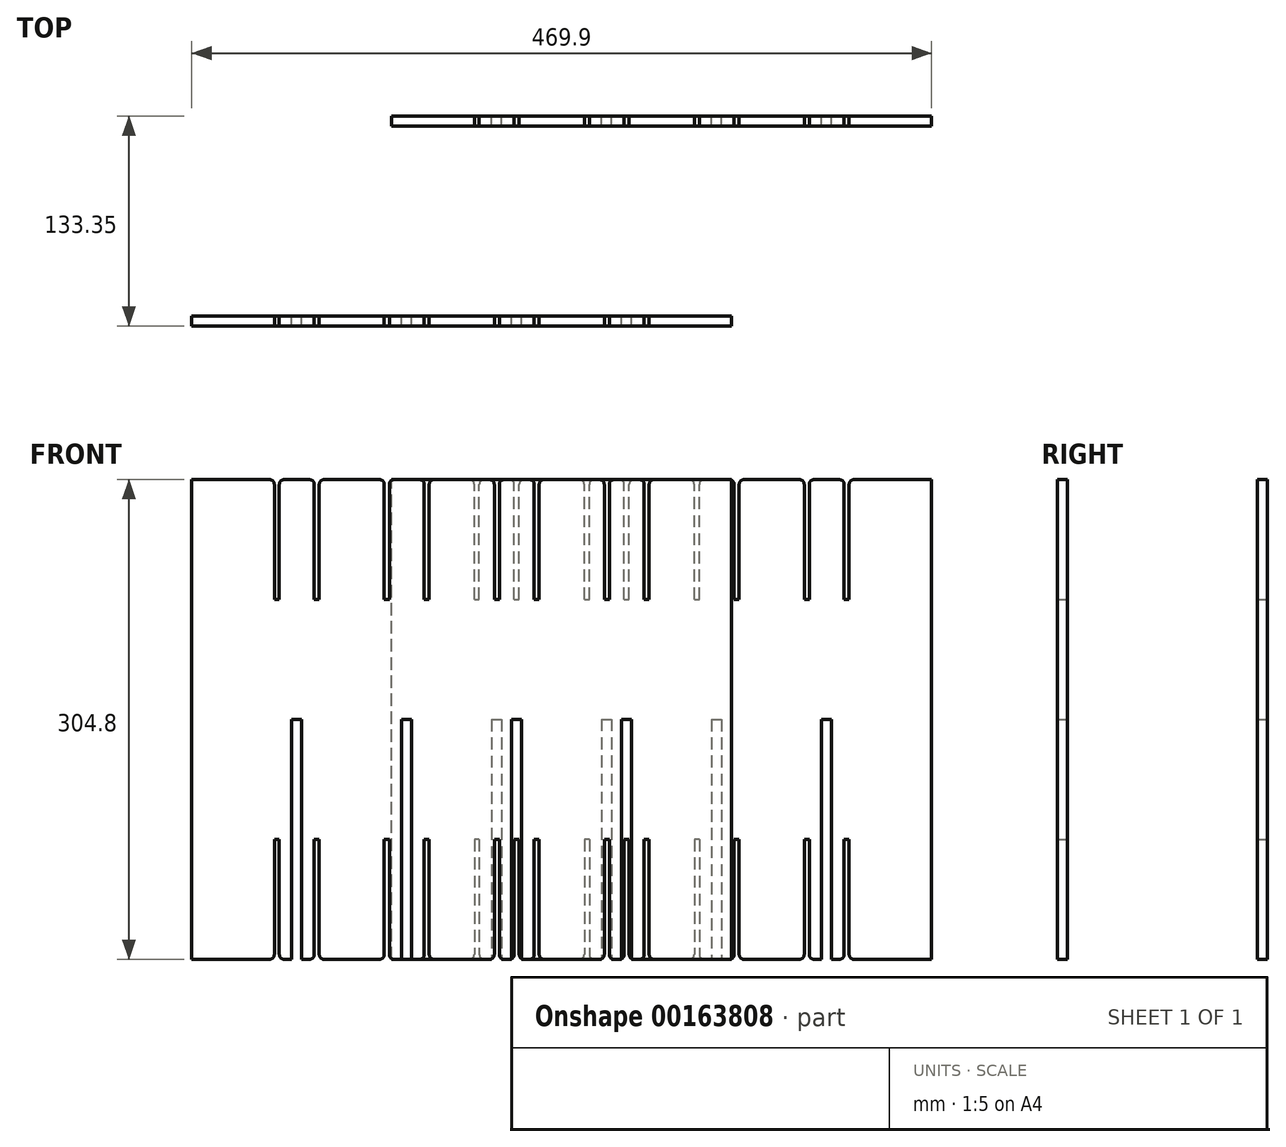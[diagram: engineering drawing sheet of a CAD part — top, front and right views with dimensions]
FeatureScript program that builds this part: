
annotation { "Feature Type Name" : "Feature", "Feature Type Description" : "" }
export const myFeature = defineFeature(function(context is Context, id is Id, definition is map)
    precondition{}
    {
        {
            var Q0;
            Q0=qCreatedBy(makeId("Front.planeOp"),FACE);
            var sketch = newSketch(context, id + "F0", { "sketchPlane" : qUnion([Q0])});
            skLineSegment(sketch, "E0.top", {"start": v(171.45, 164.84) * mm, "end": v(122.22, 164.84) * mm});
            skLineSegment(sketch, "E0.left", {"start": v(171.45, -139.96) * mm, "end": v(171.45, 164.84) * mm});
            skLineSegment(sketch, "E0.right", {"start": v(-171.45, -139.96) * mm, "end": v(-171.45, 164.84) * mm});
            skLineSegment(sketch, "E1", {"start": v(-171.45, -139.96) * mm, "end": v(-122.22, -139.96) * mm});
            skLineSegment(sketch, "E2", {"start": v(0, 0) * mm, "end": v(0, -139.96) * mm, "construction": true});
            skLineSegment(sketch, "E3.0", {"start": v(-31.75, 12.5) * mm, "end": v(-31.75, -139.96) * mm});
            skLineSegment(sketch, "E4.0", {"start": v(31.75, 12.46) * mm, "end": v(31.75, -139.96) * mm});
            skLineSegment(sketch, "E5.0", {"start": v(-38.1, 12.5) * mm, "end": v(-38.1, -139.96) * mm});
            skLineSegment(sketch, "E6.0", {"start": v(38.1, 12.46) * mm, "end": v(38.1, -139.96) * mm});
            skLineSegment(sketch, "E7.0", {"start": v(-101.6, 12.44) * mm, "end": v(-101.6, -139.96) * mm});
            skLineSegment(sketch, "E8.0", {"start": v(101.6, 12.32) * mm, "end": v(101.6, -139.96) * mm});
            skLineSegment(sketch, "E9.0", {"start": v(107.95, 12.32) * mm, "end": v(107.95, -139.96) * mm});
            skLineSegment(sketch, "E10.0", {"start": v(-107.95, 12.44) * mm, "end": v(-107.95, -139.96) * mm});
            skLineSegment(sketch, "E11", {"start": v(-107.95, 12.44) * mm, "end": v(-101.6, 12.44) * mm});
            skLineSegment(sketch, "E12", {"start": v(-38.1, 12.5) * mm, "end": v(-31.75, 12.5) * mm});
            skLineSegment(sketch, "E13", {"start": v(31.75, 12.46) * mm, "end": v(38.1, 12.46) * mm});
            skLineSegment(sketch, "E14", {"start": v(101.6, 12.32) * mm, "end": v(107.95, 12.32) * mm});
            skLineSegment(sketch, "E15.trimOffspring", {"start": v(-101.6, -139.96) * mm, "end": v(-96.85, -139.96) * mm});
            skLineSegment(sketch, "E16.trimOffspring", {"start": v(-31.75, -139.96) * mm, "end": v(-27, -139.96) * mm});
            skLineSegment(sketch, "E17.trimOffspring", {"start": v(38.1, -139.96) * mm, "end": v(42.85, -139.96) * mm});
            skLineSegment(sketch, "E18.trimOffspring", {"start": v(107.95, -139.96) * mm, "end": v(112.7, -139.96) * mm});
            skLineSegment(sketch, "E19", {"start": v(-104.77, 12.44) * mm, "end": v(-104.78, 164.84) * mm, "construction": true});
            skLineSegment(sketch, "E20", {"start": v(-34.93, 12.5) * mm, "end": v(-34.93, 164.84) * mm, "construction": true});
            skLineSegment(sketch, "E21", {"start": v(34.92, 12.46) * mm, "end": v(34.92, 164.84) * mm, "construction": true});
            skLineSegment(sketch, "E22", {"start": v(104.77, 12.32) * mm, "end": v(104.77, 164.84) * mm, "construction": true});
            skLineSegment(sketch, "E23.0", {"start": v(-93.68, 88.64) * mm, "end": v(-93.68, 161.67) * mm});
            skLineSegment(sketch, "E24.0", {"start": v(-115.87, 88.64) * mm, "end": v(-115.87, 161.67) * mm});
            skLineSegment(sketch, "E25.0", {"start": v(-119.05, 88.64) * mm, "end": v(-119.05, 161.67) * mm});
            skLineSegment(sketch, "E26.0", {"start": v(-90.5, 88.64) * mm, "end": v(-90.5, 161.67) * mm});
            skLineSegment(sketch, "E27.top", {"start": v(-119.05, 88.64) * mm, "end": v(-115.87, 88.64) * mm});
            skLineSegment(sketch, "E28.trimOffspring", {"start": v(-93.68, 88.64) * mm, "end": v(-90.5, 88.64) * mm});
            skLineSegment(sketch, "E29.trimOffspring", {"start": v(-96.85, 164.84) * mm, "end": v(-112.7, 164.84) * mm});
            skLineSegment(sketch, "E30.trimOffspring", {"start": v(-122.22, 164.84) * mm, "end": v(-171.45, 164.84) * mm});
            skPoint(sketch, "E31.visualSharp", {"position": v(-119.05, 164.84) * mm});
            skArc(sketch, "E31.filletArc", {"start": v(-119.05, 161.67) * mm, "mid": v(-119.98, 163.91) * mm, "end": v(-122.22, 164.84) * mm});
            skPoint(sketch, "E32.visualSharp", {"position": v(-115.87, 164.84) * mm});
            skArc(sketch, "E32.filletArc", {"start": v(-112.7, 164.84) * mm, "mid": v(-114.94, 163.91) * mm, "end": v(-115.87, 161.67) * mm});
            skPoint(sketch, "E33.visualSharp", {"position": v(-93.68, 164.84) * mm});
            skArc(sketch, "E33.filletArc", {"start": v(-93.68, 161.67) * mm, "mid": v(-94.6, 163.91) * mm, "end": v(-96.85, 164.84) * mm});
            skPoint(sketch, "E34.visualSharp", {"position": v(-90.5, 164.84) * mm});
            skArc(sketch, "E34.filletArc", {"start": v(-87.33, 164.84) * mm, "mid": v(-89.57, 163.91) * mm, "end": v(-90.5, 161.67) * mm});
            skLineSegment(sketch, "E35", {"start": v(-90.5, 88.64) * mm, "end": v(171.45, 88.64) * mm});
            skLineSegment(sketch, "E36.1.0.0", {"start": v(-49.2, 88.64) * mm, "end": v(-49.2, 161.67) * mm});
            skLineSegment(sketch, "E36.1.0.1", {"start": v(-46.02, 88.64) * mm, "end": v(-46.02, 161.67) * mm});
            skLineSegment(sketch, "E36.1.0.2", {"start": v(-23.83, 88.64) * mm, "end": v(-23.83, 161.67) * mm});
            skLineSegment(sketch, "E36.1.0.3", {"start": v(-20.65, 88.64) * mm, "end": v(-20.65, 161.67) * mm});
            skLineSegment(sketch, "E36.2.0.0", {"start": v(20.65, 88.64) * mm, "end": v(20.65, 161.67) * mm});
            skLineSegment(sketch, "E36.2.0.1", {"start": v(23.83, 88.64) * mm, "end": v(23.83, 161.67) * mm});
            skLineSegment(sketch, "E36.2.0.2", {"start": v(46.02, 88.64) * mm, "end": v(46.02, 161.67) * mm});
            skLineSegment(sketch, "E36.2.0.3", {"start": v(49.2, 88.64) * mm, "end": v(49.2, 161.67) * mm});
            skLineSegment(sketch, "E36.3.0.0", {"start": v(90.5, 88.64) * mm, "end": v(90.5, 161.67) * mm});
            skLineSegment(sketch, "E36.3.0.1", {"start": v(93.68, 88.64) * mm, "end": v(93.68, 161.67) * mm});
            skLineSegment(sketch, "E36.3.0.2", {"start": v(115.87, 88.64) * mm, "end": v(115.87, 161.67) * mm});
            skLineSegment(sketch, "E36.3.0.3", {"start": v(119.05, 88.64) * mm, "end": v(119.05, 161.67) * mm});
            skLineSegment(sketch, "E36.direction1", {"start": v(-119.05, 88.64) * mm, "end": v(-49.2, 88.64) * mm, "construction": true});
            skPoint(sketch, "E37.orphan", {"position": v(-49.2, 161.67) * mm});
            skPoint(sketch, "E38.orphan", {"position": v(-46.02, 161.67) * mm});
            skPoint(sketch, "E39.orphan", {"position": v(-23.83, 161.67) * mm});
            skPoint(sketch, "E40.orphan", {"position": v(-20.65, 161.67) * mm});
            skPoint(sketch, "E41.orphan", {"position": v(20.65, 161.67) * mm});
            skPoint(sketch, "E42.orphan", {"position": v(23.83, 161.67) * mm});
            skPoint(sketch, "E43.orphan", {"position": v(46.02, 161.67) * mm});
            skPoint(sketch, "E44.orphan", {"position": v(49.2, 161.67) * mm});
            skPoint(sketch, "E45.orphan", {"position": v(90.5, 161.67) * mm});
            skPoint(sketch, "E46.orphan", {"position": v(93.68, 161.67) * mm});
            skPoint(sketch, "E47.orphan", {"position": v(115.87, 161.67) * mm});
            skPoint(sketch, "E48.orphan", {"position": v(119.05, 161.67) * mm});
            skLineSegment(sketch, "E49.trimOffspring", {"start": v(112.7, 164.84) * mm, "end": v(96.85, 164.84) * mm});
            skLineSegment(sketch, "E50.trimOffspring", {"start": v(87.33, 164.84) * mm, "end": v(52.37, 164.84) * mm});
            skLineSegment(sketch, "E51.trimOffspring", {"start": v(42.85, 164.84) * mm, "end": v(27, 164.84) * mm});
            skLineSegment(sketch, "E52.trimOffspring", {"start": v(17.48, 164.84) * mm, "end": v(-17.48, 164.84) * mm});
            skLineSegment(sketch, "E53.trimOffspring", {"start": v(-27, 164.84) * mm, "end": v(-42.85, 164.84) * mm});
            skLineSegment(sketch, "E54.trimOffspring", {"start": v(-52.37, 164.84) * mm, "end": v(-87.33, 164.84) * mm});
            skPoint(sketch, "E55.visualSharp", {"position": v(-49.2, 164.84) * mm});
            skArc(sketch, "E55.filletArc", {"start": v(-49.2, 161.67) * mm, "mid": v(-50.13, 163.91) * mm, "end": v(-52.37, 164.84) * mm});
            skPoint(sketch, "E56.visualSharp", {"position": v(-46.02, 164.84) * mm});
            skArc(sketch, "E56.filletArc", {"start": v(-42.85, 164.84) * mm, "mid": v(-45.1, 163.91) * mm, "end": v(-46.02, 161.67) * mm});
            skPoint(sketch, "E57.visualSharp", {"position": v(-23.83, 164.84) * mm});
            skArc(sketch, "E57.filletArc", {"start": v(-23.83, 161.67) * mm, "mid": v(-24.76, 163.91) * mm, "end": v(-27, 164.84) * mm});
            skPoint(sketch, "E58.visualSharp", {"position": v(-20.65, 164.84) * mm});
            skArc(sketch, "E58.filletArc", {"start": v(-17.48, 164.84) * mm, "mid": v(-19.72, 163.91) * mm, "end": v(-20.65, 161.67) * mm});
            skPoint(sketch, "E59.visualSharp", {"position": v(20.65, 164.84) * mm});
            skArc(sketch, "E59.filletArc", {"start": v(20.65, 161.67) * mm, "mid": v(19.72, 163.91) * mm, "end": v(17.48, 164.84) * mm});
            skPoint(sketch, "E60.visualSharp", {"position": v(23.83, 164.84) * mm});
            skArc(sketch, "E60.filletArc", {"start": v(27, 164.84) * mm, "mid": v(24.76, 163.91) * mm, "end": v(23.83, 161.67) * mm});
            skPoint(sketch, "E61.visualSharp", {"position": v(46.02, 164.84) * mm});
            skArc(sketch, "E61.filletArc", {"start": v(46.02, 161.67) * mm, "mid": v(45.1, 163.91) * mm, "end": v(42.85, 164.84) * mm});
            skPoint(sketch, "E62.visualSharp", {"position": v(49.2, 164.84) * mm});
            skArc(sketch, "E62.filletArc", {"start": v(52.37, 164.84) * mm, "mid": v(50.13, 163.91) * mm, "end": v(49.2, 161.67) * mm});
            skPoint(sketch, "E63.visualSharp", {"position": v(90.5, 164.84) * mm});
            skArc(sketch, "E63.filletArc", {"start": v(90.5, 161.67) * mm, "mid": v(89.57, 163.91) * mm, "end": v(87.33, 164.84) * mm});
            skPoint(sketch, "E64.visualSharp", {"position": v(93.68, 164.84) * mm});
            skArc(sketch, "E64.filletArc", {"start": v(96.85, 164.84) * mm, "mid": v(94.6, 163.91) * mm, "end": v(93.68, 161.67) * mm});
            skPoint(sketch, "E65.visualSharp", {"position": v(115.87, 164.84) * mm});
            skArc(sketch, "E65.filletArc", {"start": v(115.87, 161.67) * mm, "mid": v(114.94, 163.91) * mm, "end": v(112.7, 164.84) * mm});
            skPoint(sketch, "E66.visualSharp", {"position": v(119.05, 164.84) * mm});
            skArc(sketch, "E66.filletArc", {"start": v(122.22, 164.84) * mm, "mid": v(119.98, 163.91) * mm, "end": v(119.05, 161.67) * mm});
            skLineSegment(sketch, "E67.MirrorCS", {"start": v(-119.05, -63.76) * mm, "end": v(-119.05, -136.78) * mm});
            skLineSegment(sketch, "E68.MirrorCS", {"start": v(-115.87, -63.76) * mm, "end": v(-115.87, -136.78) * mm});
            skLineSegment(sketch, "E69.MirrorCS", {"start": v(-93.68, -63.76) * mm, "end": v(-93.68, -136.78) * mm});
            skLineSegment(sketch, "E70.MirrorCS", {"start": v(-90.5, -63.76) * mm, "end": v(-90.5, -136.78) * mm});
            skLineSegment(sketch, "E71.MirrorCS", {"start": v(-49.2, -63.76) * mm, "end": v(-49.2, -136.78) * mm});
            skLineSegment(sketch, "E72.MirrorCS", {"start": v(-46.02, -63.76) * mm, "end": v(-46.02, -136.78) * mm});
            skLineSegment(sketch, "E73.MirrorCS", {"start": v(-23.83, -63.76) * mm, "end": v(-23.83, -136.78) * mm});
            skLineSegment(sketch, "E74.MirrorCS", {"start": v(-20.65, -63.76) * mm, "end": v(-20.65, -136.78) * mm});
            skLineSegment(sketch, "E75.MirrorCS", {"start": v(20.65, -63.76) * mm, "end": v(20.65, -136.78) * mm});
            skLineSegment(sketch, "E76.MirrorCS", {"start": v(23.83, -63.76) * mm, "end": v(23.83, -136.78) * mm});
            skLineSegment(sketch, "E77.MirrorCS", {"start": v(46.02, -63.76) * mm, "end": v(46.02, -136.78) * mm});
            skLineSegment(sketch, "E78.MirrorCS", {"start": v(49.2, -63.76) * mm, "end": v(49.2, -136.78) * mm});
            skLineSegment(sketch, "E79.MirrorCS", {"start": v(90.5, -63.76) * mm, "end": v(90.5, -136.78) * mm});
            skLineSegment(sketch, "E80.MirrorCS", {"start": v(93.68, -63.76) * mm, "end": v(93.68, -136.78) * mm});
            skLineSegment(sketch, "E81.MirrorCS", {"start": v(115.87, -63.76) * mm, "end": v(115.87, -136.78) * mm});
            skLineSegment(sketch, "E82.MirrorCS", {"start": v(119.05, -63.76) * mm, "end": v(119.05, -136.78) * mm});
            skPoint(sketch, "E83.orphan", {"position": v(-119.05, -136.78) * mm});
            skPoint(sketch, "E84.orphan", {"position": v(-115.87, -136.78) * mm});
            skPoint(sketch, "E85.orphan", {"position": v(-93.68, -136.78) * mm});
            skPoint(sketch, "E86.orphan", {"position": v(-90.5, -136.78) * mm});
            skPoint(sketch, "E87.orphan", {"position": v(-49.2, -136.78) * mm});
            skPoint(sketch, "E88.orphan", {"position": v(-46.02, -136.78) * mm});
            skPoint(sketch, "E89.orphan", {"position": v(-20.65, -136.78) * mm});
            skPoint(sketch, "E90.orphan", {"position": v(-23.83, -136.78) * mm});
            skPoint(sketch, "E91.orphan", {"position": v(20.65, -136.78) * mm});
            skPoint(sketch, "E92.orphan", {"position": v(23.83, -136.78) * mm});
            skPoint(sketch, "E93.orphan", {"position": v(46.02, -136.78) * mm});
            skPoint(sketch, "E94.orphan", {"position": v(49.2, -136.78) * mm});
            skPoint(sketch, "E95.orphan", {"position": v(90.5, -136.78) * mm});
            skPoint(sketch, "E96.orphan", {"position": v(93.68, -136.78) * mm});
            skPoint(sketch, "E97.orphan", {"position": v(115.87, -136.78) * mm});
            skPoint(sketch, "E98.orphan", {"position": v(119.05, -136.78) * mm});
            skLineSegment(sketch, "E99", {"start": v(119.05, -63.76) * mm, "end": v(115.87, -63.76) * mm});
            skLineSegment(sketch, "E100", {"start": v(93.68, -63.76) * mm, "end": v(90.5, -63.76) * mm});
            skLineSegment(sketch, "E101", {"start": v(49.2, -63.76) * mm, "end": v(46.02, -63.76) * mm});
            skLineSegment(sketch, "E102", {"start": v(23.83, -63.76) * mm, "end": v(20.65, -63.76) * mm});
            skLineSegment(sketch, "E103", {"start": v(-20.65, -63.76) * mm, "end": v(-23.83, -63.76) * mm});
            skLineSegment(sketch, "E104", {"start": v(-46.02, -63.76) * mm, "end": v(-49.2, -63.76) * mm});
            skLineSegment(sketch, "E105", {"start": v(-90.5, -63.76) * mm, "end": v(-93.68, -63.76) * mm});
            skLineSegment(sketch, "E106", {"start": v(-115.87, -63.76) * mm, "end": v(-119.05, -63.76) * mm});
            skLineSegment(sketch, "E107.trimOffspring", {"start": v(-112.7, -139.96) * mm, "end": v(-107.95, -139.96) * mm});
            skLineSegment(sketch, "E108.trimOffspring", {"start": v(-87.33, -139.96) * mm, "end": v(-52.37, -139.96) * mm});
            skLineSegment(sketch, "E109.trimOffspring", {"start": v(-42.85, -139.96) * mm, "end": v(-38.1, -139.96) * mm});
            skLineSegment(sketch, "E110.trimOffspring", {"start": v(-17.48, -139.96) * mm, "end": v(17.48, -139.96) * mm});
            skLineSegment(sketch, "E111.trimOffspring", {"start": v(27, -139.96) * mm, "end": v(31.75, -139.96) * mm});
            skLineSegment(sketch, "E112.trimOffspring", {"start": v(52.37, -139.96) * mm, "end": v(87.33, -139.96) * mm});
            skLineSegment(sketch, "E113.trimOffspring", {"start": v(96.85, -139.96) * mm, "end": v(101.6, -139.96) * mm});
            skLineSegment(sketch, "E114.trimOffspring", {"start": v(122.22, -139.96) * mm, "end": v(171.45, -139.96) * mm});
            skPoint(sketch, "E115.visualSharp", {"position": v(-119.05, -139.96) * mm});
            skArc(sketch, "E115.filletArc", {"start": v(-122.22, -139.96) * mm, "mid": v(-119.98, -139.03) * mm, "end": v(-119.05, -136.78) * mm});
            skPoint(sketch, "E116.visualSharp", {"position": v(-115.87, -139.96) * mm});
            skArc(sketch, "E116.filletArc", {"start": v(-115.87, -136.78) * mm, "mid": v(-114.94, -139.03) * mm, "end": v(-112.7, -139.96) * mm});
            skPoint(sketch, "E117.visualSharp", {"position": v(-93.68, -139.96) * mm});
            skArc(sketch, "E117.filletArc", {"start": v(-96.85, -139.96) * mm, "mid": v(-94.6, -139.03) * mm, "end": v(-93.68, -136.78) * mm});
            skPoint(sketch, "E118.visualSharp", {"position": v(-90.5, -139.96) * mm});
            skArc(sketch, "E118.filletArc", {"start": v(-90.5, -136.78) * mm, "mid": v(-89.57, -139.03) * mm, "end": v(-87.33, -139.96) * mm});
            skPoint(sketch, "E119.visualSharp", {"position": v(-49.2, -139.96) * mm});
            skArc(sketch, "E119.filletArc", {"start": v(-52.37, -139.96) * mm, "mid": v(-50.13, -139.03) * mm, "end": v(-49.2, -136.78) * mm});
            skPoint(sketch, "E120.visualSharp", {"position": v(-46.02, -139.96) * mm});
            skArc(sketch, "E120.filletArc", {"start": v(-46.02, -136.78) * mm, "mid": v(-45.1, -139.03) * mm, "end": v(-42.85, -139.96) * mm});
            skPoint(sketch, "E121.visualSharp", {"position": v(-23.83, -139.96) * mm});
            skArc(sketch, "E121.filletArc", {"start": v(-27, -139.96) * mm, "mid": v(-24.76, -139.03) * mm, "end": v(-23.83, -136.78) * mm});
            skPoint(sketch, "E122.visualSharp", {"position": v(-20.65, -139.96) * mm});
            skArc(sketch, "E122.filletArc", {"start": v(-20.65, -136.78) * mm, "mid": v(-19.72, -139.03) * mm, "end": v(-17.48, -139.96) * mm});
            skPoint(sketch, "E123.visualSharp", {"position": v(20.65, -139.96) * mm});
            skArc(sketch, "E123.filletArc", {"start": v(17.48, -139.96) * mm, "mid": v(19.72, -139.03) * mm, "end": v(20.65, -136.78) * mm});
            skPoint(sketch, "E124.visualSharp", {"position": v(23.83, -139.96) * mm});
            skArc(sketch, "E124.filletArc", {"start": v(23.83, -136.78) * mm, "mid": v(24.76, -139.03) * mm, "end": v(27, -139.96) * mm});
            skPoint(sketch, "E125.visualSharp", {"position": v(46.02, -139.96) * mm});
            skArc(sketch, "E125.filletArc", {"start": v(42.85, -139.96) * mm, "mid": v(45.1, -139.03) * mm, "end": v(46.02, -136.78) * mm});
            skPoint(sketch, "E126.visualSharp", {"position": v(49.2, -139.96) * mm});
            skArc(sketch, "E126.filletArc", {"start": v(49.2, -136.78) * mm, "mid": v(50.13, -139.03) * mm, "end": v(52.37, -139.96) * mm});
            skPoint(sketch, "E127.visualSharp", {"position": v(90.5, -139.96) * mm});
            skArc(sketch, "E127.filletArc", {"start": v(87.33, -139.96) * mm, "mid": v(89.57, -139.03) * mm, "end": v(90.5, -136.78) * mm});
            skPoint(sketch, "E128.visualSharp", {"position": v(93.68, -139.96) * mm});
            skArc(sketch, "E128.filletArc", {"start": v(93.68, -136.78) * mm, "mid": v(94.6, -139.03) * mm, "end": v(96.85, -139.96) * mm});
            skPoint(sketch, "E129.visualSharp", {"position": v(115.87, -139.96) * mm});
            skArc(sketch, "E129.filletArc", {"start": v(112.7, -139.96) * mm, "mid": v(114.94, -139.03) * mm, "end": v(115.87, -136.78) * mm});
            skPoint(sketch, "E130.visualSharp", {"position": v(119.05, -139.96) * mm});
            skArc(sketch, "E130.filletArc", {"start": v(119.05, -136.78) * mm, "mid": v(119.98, -139.03) * mm, "end": v(122.22, -139.96) * mm});
            skSolve(sketch);
        }
        {
            var Q0;
            Q0=qSketchRegion(id+"F0",true);
            extrude(context, id + "F1", {"entities" : qUnion([Q0]), "depth" : 6.35 * mm});
        }
        {
            var Q0;
            Q0=makeQuery(id+"F1.opExtrude","SWEPT_BODY",BODY,{"disambiguationData":[OSD([sQuery(id+"F0.wireOp",EDGE,"E0.bottom"),sQuery(id+"F0.wireOp",EDGE,"E0.top"),sQuery(id+"F0.wireOp",EDGE,"E0.left"),sQuery(id+"F0.wireOp",EDGE,"E0.right"),sQuery(id+"F0.wireOp",EDGE,"49b6419c-066e-40a3-a9b6-46c6d8486991.0"),sQuery(id+"F0.wireOp",EDGE,"825d07e1-008b-4de1-a4c6-aa6856715f16.0"),sQuery(id+"F0.wireOp",EDGE,"80cf8d0a-95a8-4f27-8c03-78616ae10c00.0"),sQuery(id+"F0.wireOp",EDGE,"9ce196c6-379f-460e-b07e-a7848fd94a840.MirrorCS"),sQuery(id+"F0.wireOp",EDGE,"a790c54b-d526-4599-92cf-5bcef03dacb40.MirrorCS"),sQuery(id+"F0.wireOp",EDGE,"a6c10973-b173-4784-8a2a-c612807bb61a0.MirrorCS"),sQuery(id+"F0.wireOp",EDGE,"hI0ua8yq-pAiN-Zqis-rnas-r4IpQ35SmrFf"),sQuery(id+"F0.wireOp",EDGE,"8b27e6ab-4e84-4d1c-8f7e-6c63eb4c60d4.trimOffspring"),sQuery(id+"F0.wireOp",EDGE,"9b0236e0-085c-400d-b6b2-96521030d671.trimOffspring"),sQuery(id+"F0.wireOp",EDGE,"4419f990-c438-4735-966b-0679363aa725.trimOffspring"),sQuery(id+"F0.wireOp",EDGE,"14cc0a87-21bd-4a9c-bf05-2e9787704ba6.trimOffspring"),sQuery(id+"F0.wireOp",EDGE,"cf1f3b0f-2c8c-481f-9d2d-5b025f7046bb.trimOffspring")])]});
            transform(context, id + "F2", {"entities" : qUnion([Q0]), "transformType" : TransformType.TRANSLATION_3D, "dx" : 127 * mm, "dy" : 127 * mm, "dz" : 0 * mm, "makeCopy" : true});
        }
    });
